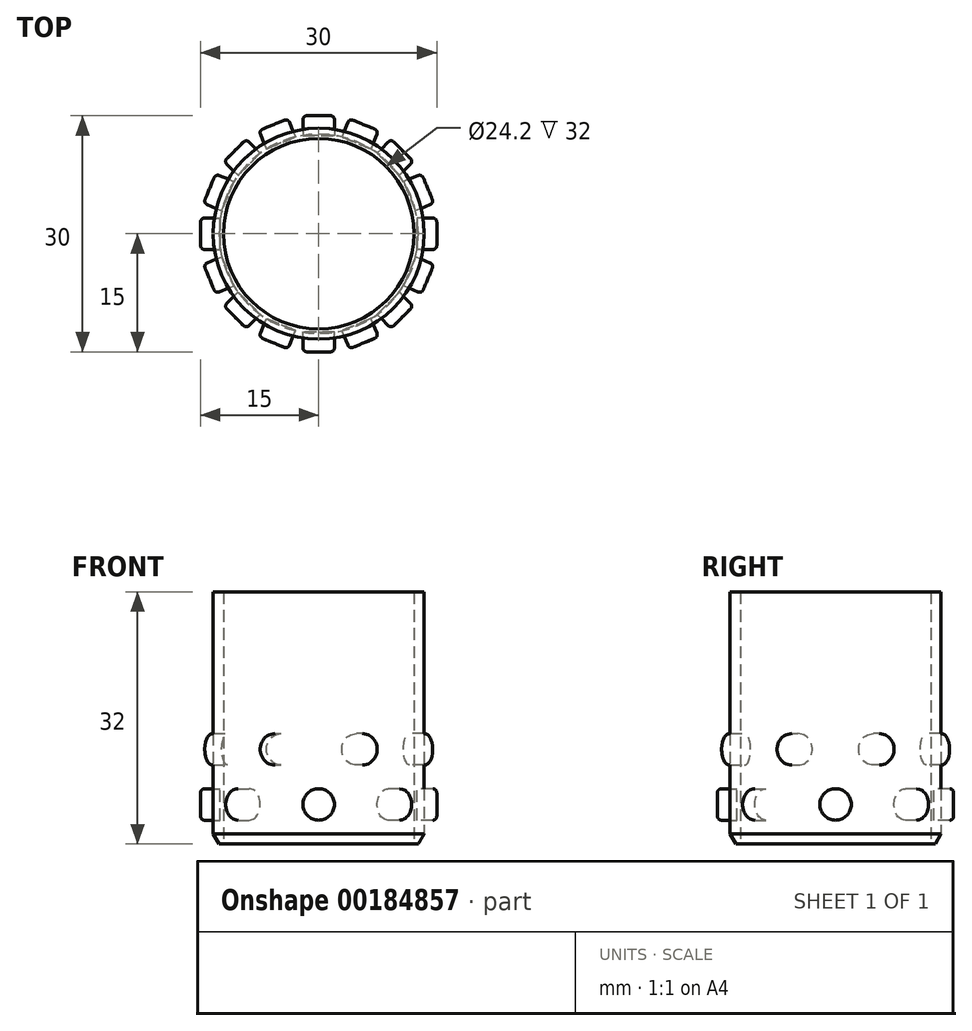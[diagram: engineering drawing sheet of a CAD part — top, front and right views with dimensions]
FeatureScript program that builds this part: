
annotation { "Feature Type Name" : "Feature", "Feature Type Description" : "" }
export const myFeature = defineFeature(function(context is Context, id is Id, definition is map)
    precondition{}
    {
        {
            var Q0;
            Q0=qCreatedBy(makeId("Top.planeOp"),FACE);
            var sketch = newSketch(context, id + "F0", { "sketchPlane" : qUnion([Q0])});
            skCircle(sketch, "E0", {"center": v(0, 0) * mm, "radius": 13.4 * mm});
            skCircle(sketch, "E1", {"center": v(0, 0) * mm, "radius": 12.1 * mm});
            skSolve(sketch);
        }
        {
            var Q0;
            Q0 = qSketchRegion(id + "F0", true);
            extrude(context, id + "F1", {"entities" : qUnion([Q0]), "depth" : 32 * mm});
        }
        {
            var Q0;
            Q0=qCreatedBy(makeId("Front.planeOp"),FACE);
            var sketch = newSketch(context, id + "F2", { "sketchPlane" : qUnion([Q0])});
            skCircle(sketch, "E2", {"center": v(0, 0) * mm, "radius": 2 * mm});
            skSolve(sketch);
        }
        {
            var Q0;
            Q0 = qSketchRegion(id + "F2", true);
            extrude(context, id + "F3", {"entities" : qUnion([Q0]), "depth" : 2.5 * mm});
        }
        {
            var Q0;
            Q0=makeQuery(id+"F3.opExtrude","CAP_EDGE",EDGE,{"disambiguationData":[OSD([sQuery(id+"F2.wireOp",EDGE,"E2")])],"isStart":false});
            fillet(context, id + "F4", {"entities" : qUnion([Q0]), "radius" : .5 * mm, "tangentPropagation" : true, "allowEdgeOverflow" : false});
        }
        {
            var Q0;
            Q0=makeQuery(id+"F3.opExtrude","SWEPT_BODY",BODY,{"disambiguationData":[OSD([sQuery(id+"F2.wireOp",EDGE,"E2")])]});
            transform(context, id + "F5", {"entities" : qUnion([Q0]), "transformType" : TransformType.TRANSLATION_3D, "dx" : 0 * mm, "dy" : -12.5 * mm, "dz" : 5 * mm, "makeCopy" : false});
        }
        {
            var Q0;
            Q0=makeQuery(id+"F3.opExtrude","SWEPT_BODY",BODY,{"disambiguationData":[OSD([sQuery(id+"F2.wireOp",EDGE,"E2")])]});
            var Q1;
            Q1=makeQuery(id+"F1.opExtrude","SWEPT_FACE",FACE,{"disambiguationData":[OSD([sQuery(id+"F0.wireOp",EDGE,"E0")])]});
            var Q2;
            Q2=makeQuery(id+"F1.opExtrude","SWEPT_BODY",BODY,{"disambiguationData":[OSD([sQuery(id+"F0.wireOp",EDGE,"E0"),sQuery(id+"F0.wireOp",EDGE,"E1")])]});
            circularPattern(context, id + "F6", {"entities" : qUnion([Q0]), "axis" : qUnion([Q1]), "angle" : 360 * degree, "instanceCount" : 8, "equalSpace" : true});
        }
        {
            var Q0;
            Q0=makeQuery(id+"F3.opExtrude","SWEPT_BODY",BODY,{"disambiguationData":[OSD([sQuery(id+"F2.wireOp",EDGE,"E2")])]});
            transform(context, id + "F7", {"entities" : qUnion([Q0]), "transformType" : TransformType.TRANSLATION_3D, "dx" : 0 * mm, "dy" : 0 * mm, "dz" : 7 * mm, "makeCopy" : true});
        }
        {
            var Q0;
            Q0=makeQuery(id+"F7.opPattern","COPY",BODY,{"derivedFrom":makeQuery(id+"F3.opExtrude","SWEPT_BODY",BODY,{"disambiguationData":[OSD([sQuery(id+"F2.wireOp",EDGE,"E2")])]}),"instanceName":"1"});
            var Q1;
            Q1=makeQuery(id+"F1.opExtrude","SWEPT_FACE",FACE,{"disambiguationData":[OSD([sQuery(id+"F0.wireOp",EDGE,"E0")])]});
            transform(context, id + "F8", {"entities" : qUnion([Q0]), "transformType" : TransformType.ROTATION, "transformAxis" : qUnion([Q1]), "angle" : 22.5 * degree, "makeCopy" : false});
        }
        {
            var Q0;
            Q0=makeQuery(id+"F7.opPattern","COPY",BODY,{"derivedFrom":makeQuery(id+"F3.opExtrude","SWEPT_BODY",BODY,{"disambiguationData":[OSD([sQuery(id+"F2.wireOp",EDGE,"E2")])]}),"instanceName":"1"});
            var Q1;
            Q1=makeQuery(id+"F1.opExtrude","SWEPT_FACE",FACE,{"disambiguationData":[OSD([sQuery(id+"F0.wireOp",EDGE,"E0")])]});
            circularPattern(context, id + "F9", {"entities" : qUnion([Q0]), "axis" : qUnion([Q1]), "angle" : 360 * degree, "instanceCount" : 8, "equalSpace" : true});
        }
        {
            var Q0;
            Q0=makeQuery(id+"F1.opExtrude","CAP_EDGE",EDGE,{"disambiguationData":[OSD([sQuery(id+"F0.wireOp",EDGE,"E0")])],"isStart":true});
            chamfer(context, id + "F10", {"entities" : qUnion([Q0]), "chamferType" : ChamferType.TWO_OFFSETS, "width1" : 1.25 * mm, "oppositeDirection" : false, "width2" : .75 * mm, "tangentPropagation" : true});
        }
    });
